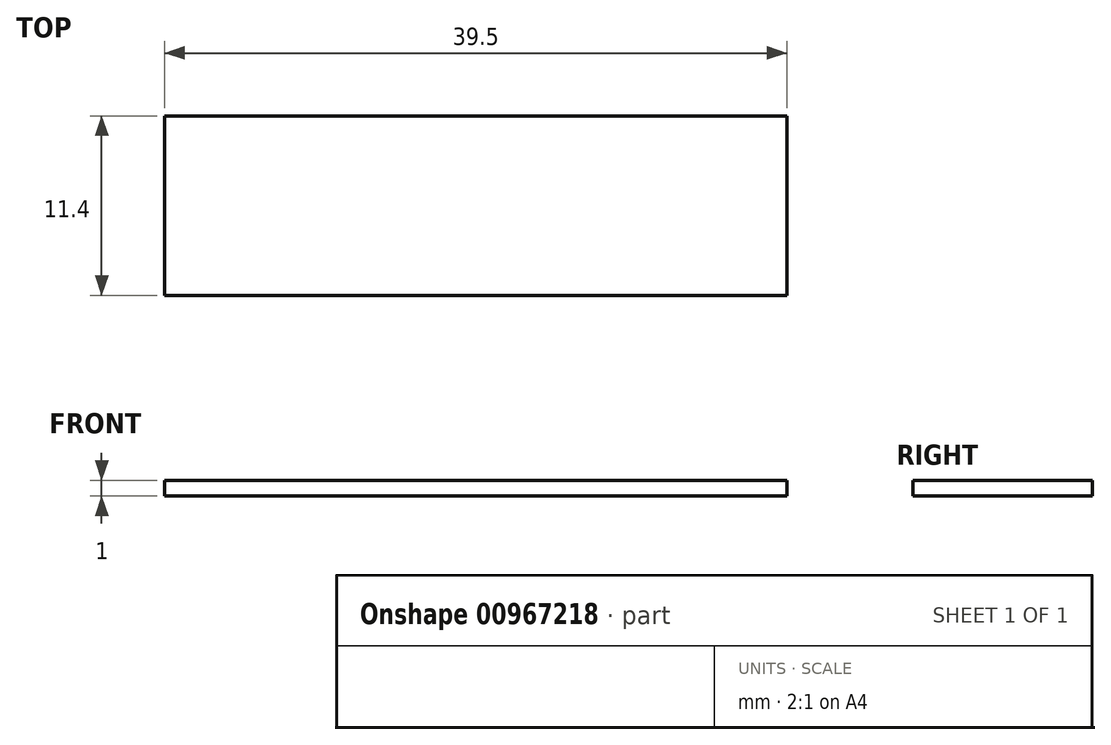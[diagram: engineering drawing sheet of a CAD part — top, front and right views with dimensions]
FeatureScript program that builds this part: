
annotation { "Feature Type Name" : "Feature", "Feature Type Description" : "" }
export const myFeature = defineFeature(function(context is Context, id is Id, definition is map)
    precondition{}
    {
        {
            var Q0;
            Q0=qCreatedBy(makeId("Top.planeOp"),FACE);
            var sketch = newSketch(context, id + "F0", { "sketchPlane" : qUnion([Q0])});
            skLineSegment(sketch, "E0.bottom", {"start": v(-19.75, 5.7) * mm, "end": v(19.75, 5.7) * mm});
            skLineSegment(sketch, "E0.top", {"start": v(-19.75, -5.7) * mm, "end": v(19.75, -5.7) * mm});
            skLineSegment(sketch, "E0.left", {"start": v(-19.75, 5.7) * mm, "end": v(-19.75, -5.7) * mm});
            skLineSegment(sketch, "E0.right", {"start": v(19.75, 5.7) * mm, "end": v(19.75, -5.7) * mm});
            skPoint(sketch, "E0.middle", {"position": v(0, 0) * mm});
            skSolve(sketch);
        }
        {
            var Q0;
            Q0 = qSketchRegion(id + "F0", true);
            extrude(context, id + "F1", {"entities" : qUnion([Q0]), "depth" : 1 * mm, "offsetDistance" : 25 * mm});
        }
    });
